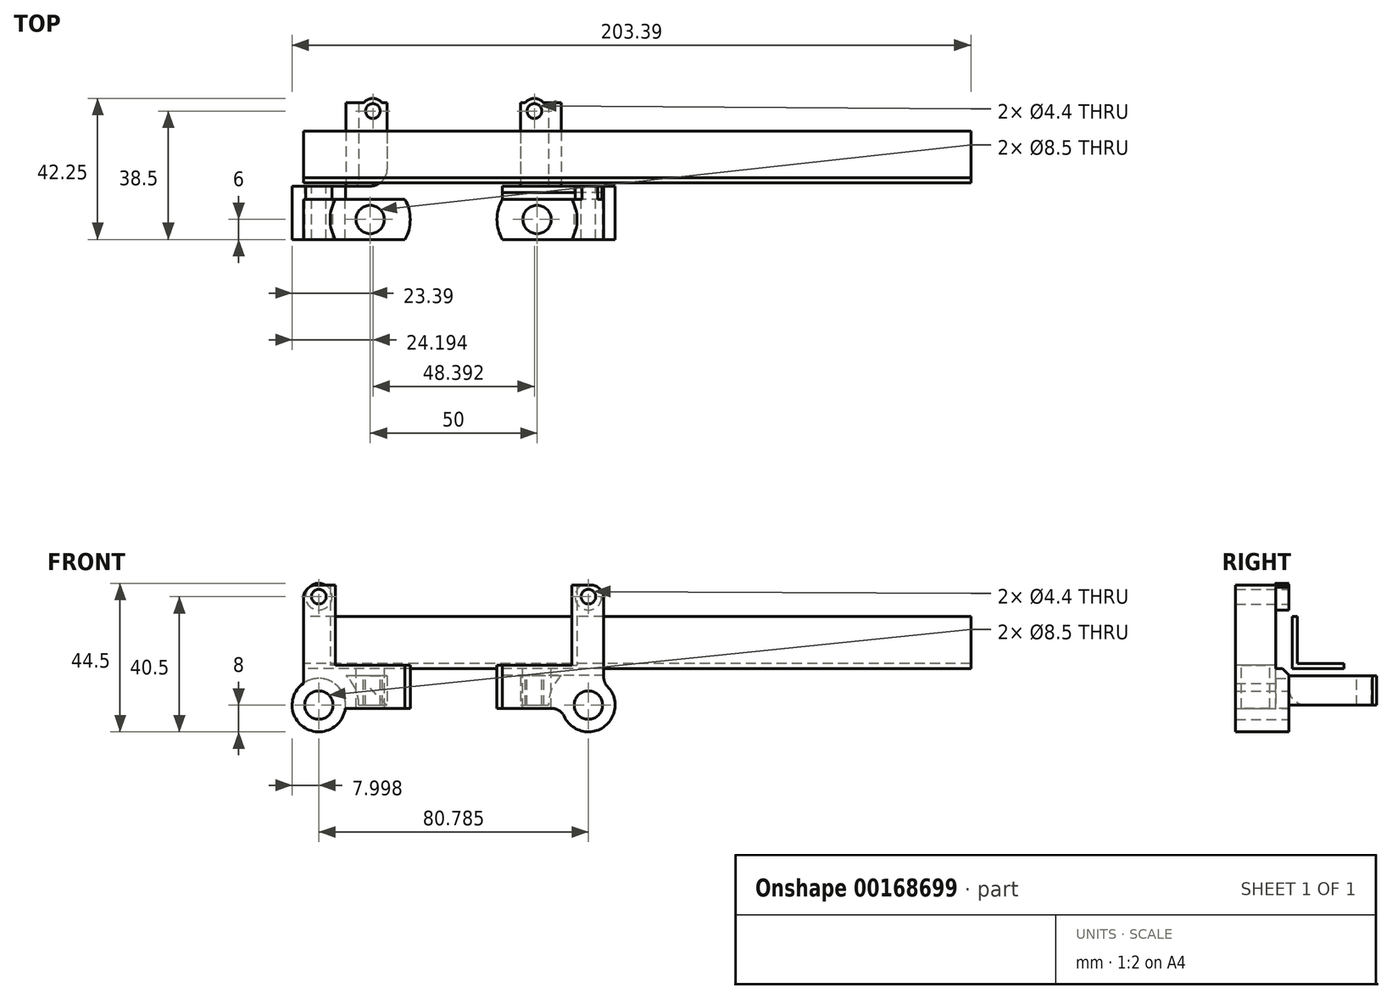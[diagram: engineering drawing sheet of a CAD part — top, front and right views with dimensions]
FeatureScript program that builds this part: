
annotation { "Feature Type Name" : "Feature", "Feature Type Description" : "" }
export const myFeature = defineFeature(function(context is Context, id is Id, definition is map)
    precondition{}
    {
        {
            var Q0;
            Q0=qCreatedBy(makeId("Right.planeOp"),FACE);
            var sketch = newSketch(context, id + "F0", { "sketchPlane" : qUnion([Q0])});
            skLineSegment(sketch, "E0", {"start": v(0, 0) * mm, "end": v(0, 15.5) * mm});
            skLineSegment(sketch, "E1", {"start": v(0, 15.5) * mm, "end": v(1.5, 15.5) * mm});
            skLineSegment(sketch, "E2", {"start": v(1.5, 15.5) * mm, "end": v(1.5, 1.5) * mm});
            skLineSegment(sketch, "E3", {"start": v(1.5, 1.5) * mm, "end": v(15.5, 1.5) * mm});
            skLineSegment(sketch, "E4", {"start": v(15.5, 1.5) * mm, "end": v(15.5, 0) * mm});
            skLineSegment(sketch, "E5", {"start": v(15.5, 0) * mm, "end": v(0, 0) * mm});
            skSolve(sketch);
        }
        {
            var Q0;
            Q0 = qSketchRegion(id + "F0", true);
            extrude(context, id + "F1", {"entities" : qUnion([Q0]), "depth" : 200 * mm, "offsetDistance" : 25 * mm});
        }
        {
            var Q0;
            Q0=qCreatedBy(makeId("Top.planeOp"),FACE);
            var sketch = newSketch(context, id + "F2", { "sketchPlane" : qUnion([Q0])});
            skCircle(sketch, "E6", {"center": v(20, -11) * mm, "radius": 11 * mm, "construction": true});
            skCircle(sketch, "E7", {"center": v(70, -11) * mm, "radius": 11 * mm, "construction": true});
            skCircle(sketch, "E8", {"center": v(20, -11) * mm, "radius": 4.25 * mm});
            skCircle(sketch, "E9", {"center": v(70, -11) * mm, "radius": 4.25 * mm});
            skLineSegment(sketch, "E10.bottom", {"start": v(0, -5) * mm, "end": v(90, -5) * mm});
            skLineSegment(sketch, "E10.top", {"start": v(0, -17) * mm, "end": v(90, -17) * mm});
            skLineSegment(sketch, "E10.left", {"start": v(0, -5) * mm, "end": v(0, -17) * mm});
            skLineSegment(sketch, "E10.right", {"start": v(90, -5) * mm, "end": v(90, -17) * mm});
            skPoint(sketch, "E10.middle", {"position": v(45, -11) * mm});
            skCircle(sketch, "E11", {"center": v(20, -11) * mm, "radius": 12 * mm});
            skCircle(sketch, "E12", {"center": v(70, -11) * mm, "radius": 12 * mm});
            skSolve(sketch);
        }
        {
            var Q0;
            {var subQ0=sQuery(id+"F2.wireOp",EDGE,"E10.left");Q0=makeQuery(id+"F2.imprint","IMPRINT",FACE,{"disambiguationData":[TD([[makeQuery(id+"F2.imprint","IMPRINT",EDGE,{"derivedFrom":subQ0}),1.0]])]});}
            var Q1;
            {var subQ0=sQuery(id+"F2.wireOp",EDGE,"E11");var subQ1=sQuery(id+"F2.wireOp",EDGE,"E10.bottom");var subQ2=makeQuery(id+"F2.imprint","INTERSECT",VERTEX,{"disambiguationData":[OD(1.0)],"derivedFrom":[subQ1,subQ0]});Q1=makeQuery(id+"F2.imprint","IMPRINT",FACE,{"disambiguationData":[TD([[makeQuery(id+"F2.imprint","IMPRINT",EDGE,{"disambiguationData":[TD([[subQ2,-1.0]])],"derivedFrom":subQ1}),-1.0]])]});}
            var Q2;
            {var subQ0=sQuery(id+"F2.wireOp",EDGE,"E10.right");Q2=makeQuery(id+"F2.imprint","IMPRINT",FACE,{"disambiguationData":[TD([[makeQuery(id+"F2.imprint","IMPRINT",EDGE,{"derivedFrom":subQ0}),-1.0]])]});}
            var Q3;
            Q3=makeQuery(id+"F2.imprint","IMPRINT",FACE,{"disambiguationData":[TD([[makeQuery(id+"F2.imprint","IMPRINT",EDGE,{"derivedFrom":sQuery(id+"F2.wireOp",EDGE,"E8")}),-1.0]])]});
            var Q4;
            Q4=makeQuery(id+"F2.imprint","IMPRINT",FACE,{"disambiguationData":[TD([[makeQuery(id+"F2.imprint","IMPRINT",EDGE,{"derivedFrom":sQuery(id+"F2.wireOp",EDGE,"E9")}),-1.0]])]});
            extrude(context, id + "F3", {"entities" : qUnion([Q0, Q1, Q2, Q3, Q4]), "oppositeDirection" : true, "depth" : 12 * mm, "offsetDistance" : 25 * mm, "hasSecondDirection" : true, "secondDirectionOppositeDirection" : false, "secondDirectionDepth" : 1 * mm});
        }
        {
            var Q0;
            {var subQ0=sQuery(id+"F2.wireOp",EDGE,"E10.left");Q0=makeQuery(id+"F2.imprint","IMPRINT",FACE,{"disambiguationData":[TD([[makeQuery(id+"F2.imprint","IMPRINT",EDGE,{"derivedFrom":subQ0}),1.0]])]});}
            var Q1;
            {var subQ0=sQuery(id+"F2.wireOp",EDGE,"E10.right");Q1=makeQuery(id+"F2.imprint","IMPRINT",FACE,{"disambiguationData":[TD([[makeQuery(id+"F2.imprint","IMPRINT",EDGE,{"derivedFrom":subQ0}),-1.0]])]});}
            extrude(context, id + "F4", {"entities" : qUnion([Q0, Q1]), "operationType" : NewBodyOperationType.ADD, "depth" : 25 * mm, "offsetDistance" : 25 * mm});
        }
        {
            var Q0;
            {var subQ0=sQuery(id+"F2.wireOp",EDGE,"E10.bottom");var subQ2=sQuery(id+"F2.wireOp",EDGE,"E11");Q0=makeQuery(id+"F4.boolean.opBoolean","MERGE",FACE,{"derivedFrom":[makeQuery(id+"F3.opExtrude","SWEPT_FACE",FACE,{"disambiguationData":[OSD([subQ0])]}),makeQuery(id+"F4.opExtrude","SWEPT_FACE",FACE,{"disambiguationData":[OSD([subQ0]),TDD([makeQuery(id+"F2.imprint","IMPRINT",EDGE,{"disambiguationData":[TD([[makeQuery(id+"F2.imprint","INTERSECT",VERTEX,{"derivedFrom":[subQ0,sQuery(id+"F2.wireOp",EDGE,"E10.left")]}),-1.0]])],"derivedFrom":subQ0})])]}),makeQuery(id+"F4.opExtrude","SWEPT_FACE",FACE,{"disambiguationData":[OSD([subQ0]),TDD([makeQuery(id+"F2.imprint","IMPRINT",EDGE,{"disambiguationData":[TD([[makeQuery(id+"F2.imprint","INTERSECT",VERTEX,{"disambiguationData":[OD(1.0)],"derivedFrom":[subQ0,subQ2]}),-1.0]])],"derivedFrom":subQ0})])]}),makeQuery(id+"F4.opExtrude","SWEPT_FACE",FACE,{"disambiguationData":[OSD([subQ0]),TDD([makeQuery(id+"F2.imprint","IMPRINT",EDGE,{"disambiguationData":[TD([[makeQuery(id+"F2.imprint","INTERSECT",VERTEX,{"derivedFrom":[subQ0,sQuery(id+"F2.wireOp",EDGE,"E10.right")]}),1.0]])],"derivedFrom":subQ0})])]})]});}
            var sketch = newSketch(context, id + "F5", { "sketchPlane" : qUnion([Q0])});
            skLineSegment(sketch, "E13.0.0", {"start": v(0, 1.5) * mm, "end": v(0, 15.5) * mm});
            skLineSegment(sketch, "E13.0.1", {"start": v(0, 15.5) * mm, "end": v(-200, 15.5) * mm});
            skLineSegment(sketch, "E13.0.2", {"start": v(-200, 15.5) * mm, "end": v(-200, 1.5) * mm});
            skLineSegment(sketch, "E13.0.3", {"start": v(-200, 1.5) * mm, "end": v(0, 1.5) * mm});
            skCircle(sketch, "E14", {"center": v(-4.6, 21.5) * mm, "radius": 6 * mm, "construction": true});
            skCircle(sketch, "E15", {"center": v(-4.6, 21.5) * mm, "radius": 2.2 * mm});
            skCircle(sketch, "E16", {"center": v(-85.4, 21.5) * mm, "radius": 6 * mm, "construction": true});
            skCircle(sketch, "E17", {"center": v(-85.4, 21.5) * mm, "radius": 2.2 * mm});
            skCircle(sketch, "E18", {"center": v(-4.6, 21.5) * mm, "radius": 4 * mm});
            skCircle(sketch, "E19", {"center": v(-85.4, 21.5) * mm, "radius": 4 * mm});
            skLineSegment(sketch, "E20.0", {"start": v(-200, 0) * mm, "end": v(0, 0) * mm});
            skCircle(sketch, "E21", {"center": v(-85.4, -11) * mm, "radius": 11 * mm, "construction": true});
            skCircle(sketch, "E22", {"center": v(-4.6, -11) * mm, "radius": 11 * mm, "construction": true});
            skCircle(sketch, "E23", {"center": v(-85.4, -11) * mm, "radius": 4.25 * mm});
            skCircle(sketch, "E24", {"center": v(-4.6, -11) * mm, "radius": 4.25 * mm});
            skCircle(sketch, "E25", {"center": v(-85.4, -11) * mm, "radius": 8 * mm});
            skCircle(sketch, "E26", {"center": v(-4.6, -11) * mm, "radius": 8 * mm});
            skSolve(sketch);
        }
        {
            var Q0;
            Q0=makeQuery(id+"F5.imprint","IMPRINT",FACE,{"disambiguationData":[TD([[makeQuery(id+"F5.imprint","IMPRINT",EDGE,{"derivedFrom":sQuery(id+"F5.wireOp",EDGE,"E15")}),1.0]])]});
            var Q1;
            Q1=makeQuery(id+"F5.imprint","IMPRINT",FACE,{"disambiguationData":[TD([[makeQuery(id+"F5.imprint","IMPRINT",EDGE,{"derivedFrom":sQuery(id+"F5.wireOp",EDGE,"E17")}),1.0]])]});
            extrude(context, id + "F6", {"entities" : qUnion([Q0, Q1]), "operationType" : NewBodyOperationType.REMOVE, "oppositeDirection" : true, "depth" : 25 * mm, "offsetDistance" : 25 * mm});
        }
        {
            var Q0;
            Q0=makeQuery(id+"F5.imprint","IMPRINT",FACE,{"disambiguationData":[TD([[makeQuery(id+"F5.imprint","IMPRINT",EDGE,{"derivedFrom":sQuery(id+"F5.wireOp",EDGE,"E15")}),-1.0]])]});
            var Q1;
            Q1=makeQuery(id+"F5.imprint","IMPRINT",FACE,{"disambiguationData":[TD([[makeQuery(id+"F5.imprint","IMPRINT",EDGE,{"derivedFrom":sQuery(id+"F5.wireOp",EDGE,"E17")}),-1.0]])]});
            extrude(context, id + "F7", {"entities" : qUnion([Q0, Q1]), "operationType" : NewBodyOperationType.ADD, "depth" : 4 * mm, "offsetDistance" : 25 * mm});
        }
        {
            var Q0;
            {var subQ1=sQuery(id+"F2.wireOp",EDGE,"E10.bottom");var subQ3=makeQuery(id+"F3.opExtrude","CAP_EDGE",EDGE,{"disambiguationData":[OSD([subQ1])],"isStart":false});var subQ8=sQuery(id+"F5.wireOp",EDGE,"E23");var subQ9=makeQuery(id+"F5.imprint","INTERSECT",VERTEX,{"disambiguationData":[OD(0.0)],"derivedFrom":[subQ3,subQ8]});Q0=makeQuery(id+"F5.imprint","IMPRINT",FACE,{"disambiguationData":[TD([[makeQuery(id+"F5.imprint","IMPRINT",EDGE,{"disambiguationData":[TD([[subQ9,-1.0]])],"derivedFrom":subQ8}),-1.0]])]});}
            var Q1;
            {var subQ1=sQuery(id+"F2.wireOp",EDGE,"E10.bottom");var subQ3=makeQuery(id+"F3.opExtrude","CAP_EDGE",EDGE,{"disambiguationData":[OSD([subQ1])],"isStart":false});var subQ7=sQuery(id+"F5.wireOp",EDGE,"E24");var subQ8=makeQuery(id+"F5.imprint","INTERSECT",VERTEX,{"disambiguationData":[OD(0.0)],"derivedFrom":[subQ3,subQ7]});Q1=makeQuery(id+"F5.imprint","IMPRINT",FACE,{"disambiguationData":[TD([[makeQuery(id+"F5.imprint","IMPRINT",EDGE,{"disambiguationData":[TD([[subQ8,1.0]])],"derivedFrom":subQ7}),-1.0]])]});}
            var Q2;
            {var subQ0=sQuery(id+"F2.wireOp",EDGE,"E10.top");Q2=makeQuery(id+"F4.boolean.opBoolean","MERGE",FACE,{"derivedFrom":[makeQuery(id+"F3.opExtrude","SWEPT_FACE",FACE,{"disambiguationData":[OSD([subQ0])]}),makeQuery(id+"F4.opExtrude","SWEPT_FACE",FACE,{"disambiguationData":[OSD([subQ0]),TDD([makeQuery(id+"F2.imprint","IMPRINT",EDGE,{"disambiguationData":[TD([[makeQuery(id+"F2.imprint","INTERSECT",VERTEX,{"derivedFrom":[subQ0,sQuery(id+"F2.wireOp",EDGE,"E10.left")]}),-1.0]])],"derivedFrom":subQ0})])]}),makeQuery(id+"F4.opExtrude","SWEPT_FACE",FACE,{"disambiguationData":[OSD([subQ0]),TDD([makeQuery(id+"F2.imprint","IMPRINT",EDGE,{"disambiguationData":[TD([[makeQuery(id+"F2.imprint","INTERSECT",VERTEX,{"derivedFrom":[subQ0,sQuery(id+"F2.wireOp",EDGE,"E10.right")]}),1.0]])],"derivedFrom":subQ0})])]})]});}
            extrude(context, id + "F8", {"entities" : qUnion([Q0, Q1]), "operationType" : NewBodyOperationType.ADD, "endBound" : BoundingType.UP_TO_SURFACE, "oppositeDirection" : true, "depth" : 25 * mm, "endBoundEntityFace" : qUnion([Q2]), "offsetDistance" : 25 * mm});
        }
        {
            var Q0;
            {var subQ0=sQuery(id+"F5.wireOp",EDGE,"E23");var subQ1=makeQuery(id+"F3.opExtrude","CAP_EDGE",EDGE,{"disambiguationData":[OSD([sQuery(id+"F2.wireOp",EDGE,"E10.bottom")])],"isStart":false});var subQ2=makeQuery(id+"F5.imprint","INTERSECT",VERTEX,{"disambiguationData":[OD(0.0)],"derivedFrom":[subQ1,subQ0]});Q0=makeQuery(id+"F5.imprint","IMPRINT",FACE,{"disambiguationData":[TD([[makeQuery(id+"F5.imprint","IMPRINT",EDGE,{"disambiguationData":[TD([[subQ2,1.0]])],"derivedFrom":subQ0}),1.0]])]});}
            var Q1;
            {var subQ0=sQuery(id+"F5.wireOp",EDGE,"E24");var subQ1=makeQuery(id+"F3.opExtrude","CAP_EDGE",EDGE,{"disambiguationData":[OSD([sQuery(id+"F2.wireOp",EDGE,"E10.bottom")])],"isStart":false});var subQ2=makeQuery(id+"F5.imprint","INTERSECT",VERTEX,{"disambiguationData":[OD(0.0)],"derivedFrom":[subQ1,subQ0]});Q1=makeQuery(id+"F5.imprint","IMPRINT",FACE,{"disambiguationData":[TD([[makeQuery(id+"F5.imprint","IMPRINT",EDGE,{"disambiguationData":[TD([[subQ2,-1.0]])],"derivedFrom":subQ0}),1.0]])]});}
            extrude(context, id + "F9", {"entities" : qUnion([Q0, Q1]), "operationType" : NewBodyOperationType.REMOVE, "oppositeDirection" : true, "depth" : 25 * mm, "offsetDistance" : 25 * mm});
        }
        {
            var Q0;
            {var subQ0=sQuery(id+"F5.wireOp",EDGE,"E25");var subQ1=sQuery(id+"F2.wireOp",EDGE,"E10.bottom");var subQ2=makeQuery(id+"F3.opExtrude","CAP_EDGE",EDGE,{"disambiguationData":[OSD([subQ1])],"isStart":false});var subQ3=makeQuery(id+"F5.imprint","INTERSECT",VERTEX,{"derivedFrom":[subQ2,subQ0]});Q0=makeQuery(id+"F5.imprint","IMPRINT",FACE,{"disambiguationData":[TD([[makeQuery(id+"F5.imprint","IMPRINT",EDGE,{"disambiguationData":[TD([[subQ3,1.0]])],"derivedFrom":subQ2}),-1.0]])]});}
            var Q1;
            {var subQ1=sQuery(id+"F2.wireOp",EDGE,"E10.bottom");var subQ3=makeQuery(id+"F3.opExtrude","CAP_EDGE",EDGE,{"disambiguationData":[OSD([subQ1])],"isStart":false});var subQ7=sQuery(id+"F5.wireOp",EDGE,"E23");var subQ8=makeQuery(id+"F5.imprint","INTERSECT",VERTEX,{"disambiguationData":[OD(0.0)],"derivedFrom":[subQ3,subQ7]});Q1=makeQuery(id+"F5.imprint","IMPRINT",FACE,{"disambiguationData":[TD([[makeQuery(id+"F5.imprint","IMPRINT",EDGE,{"disambiguationData":[TD([[subQ8,1.0]])],"derivedFrom":subQ7}),-1.0]])]});}
            var Q2;
            {var subQ1=sQuery(id+"F2.wireOp",EDGE,"E10.bottom");var subQ3=makeQuery(id+"F3.opExtrude","CAP_EDGE",EDGE,{"disambiguationData":[OSD([subQ1])],"isStart":false});var subQ8=sQuery(id+"F5.wireOp",EDGE,"E23");var subQ9=makeQuery(id+"F5.imprint","INTERSECT",VERTEX,{"disambiguationData":[OD(0.0)],"derivedFrom":[subQ3,subQ8]});Q2=makeQuery(id+"F5.imprint","IMPRINT",FACE,{"disambiguationData":[TD([[makeQuery(id+"F5.imprint","IMPRINT",EDGE,{"disambiguationData":[TD([[subQ9,-1.0]])],"derivedFrom":subQ8}),-1.0]])]});}
            var Q3;
            {var subQ1=sQuery(id+"F2.wireOp",EDGE,"E10.bottom");var subQ3=makeQuery(id+"F3.opExtrude","CAP_EDGE",EDGE,{"disambiguationData":[OSD([subQ1])],"isStart":false});var subQ5=sQuery(id+"F5.wireOp",EDGE,"E24");var subQ6=makeQuery(id+"F5.imprint","INTERSECT",VERTEX,{"disambiguationData":[OD(0.0)],"derivedFrom":[subQ3,subQ5]});Q3=makeQuery(id+"F5.imprint","IMPRINT",FACE,{"disambiguationData":[TD([[makeQuery(id+"F5.imprint","IMPRINT",EDGE,{"disambiguationData":[TD([[subQ6,-1.0]])],"derivedFrom":subQ5}),-1.0]])]});}
            var Q4;
            {var subQ1=sQuery(id+"F2.wireOp",EDGE,"E10.bottom");var subQ3=makeQuery(id+"F3.opExtrude","CAP_EDGE",EDGE,{"disambiguationData":[OSD([subQ1])],"isStart":false});var subQ7=sQuery(id+"F5.wireOp",EDGE,"E24");var subQ8=makeQuery(id+"F5.imprint","INTERSECT",VERTEX,{"disambiguationData":[OD(0.0)],"derivedFrom":[subQ3,subQ7]});Q4=makeQuery(id+"F5.imprint","IMPRINT",FACE,{"disambiguationData":[TD([[makeQuery(id+"F5.imprint","IMPRINT",EDGE,{"disambiguationData":[TD([[subQ8,1.0]])],"derivedFrom":subQ7}),-1.0]])]});}
            extrude(context, id + "F10", {"entities" : qUnion([Q0, Q1, Q2, Q3, Q4]), "operationType" : NewBodyOperationType.ADD, "depth" : 4 * mm, "offsetDistance" : 25 * mm});
        }
        {
            var Q0;
            Q0=makeQuery(id+"F10.opExtrude","CAP_FACE",FACE,{"disambiguationData":[OSD([sQuery(id+"F2.wireOp",EDGE,"E10.bottom"),sQuery(id+"F2.wireOp",EDGE,"E10.left"),sQuery(id+"F2.wireOp",EDGE,"E10.right"),sQuery(id+"F5.wireOp",EDGE,"E20.0"),sQuery(id+"F5.wireOp",EDGE,"E23"),sQuery(id+"F5.wireOp",EDGE,"E24"),sQuery(id+"F5.wireOp",EDGE,"E25"),sQuery(id+"F5.wireOp",EDGE,"E26")])],"isStart":false});
            var sketch = newSketch(context, id + "F11", { "sketchPlane" : qUnion([Q0])});
            skCircle(sketch, "E27", {"center": v(-85.4, -11) * mm, "radius": 12 * mm});
            skCircle(sketch, "E28", {"center": v(-4.6, -11) * mm, "radius": 12 * mm});
            skLineSegment(sketch, "E29.top", {"start": v(-85.4, -2.23) * mm, "end": v(0, -2.23) * mm});
            skLineSegment(sketch, "E29.left", {"start": v(-85.4, -11) * mm, "end": v(-85.4, -2.23) * mm});
            skLineSegment(sketch, "E29.right", {"start": v(0, -11) * mm, "end": v(0, -2.23) * mm});
            skLineSegment(sketch, "E30", {"start": v(-4.6, -11) * mm, "end": v(-4.6, -2.23) * mm});
            skLineSegment(sketch, "E31", {"start": v(-4.6, -11) * mm, "end": v(-85.4, -11) * mm});
            skLineSegment(sketch, "E32.bottom", {"start": v(-65, -2.23) * mm, "end": v(-25, -2.23) * mm});
            skLineSegment(sketch, "E32.top", {"start": v(-65, -11) * mm, "end": v(-25, -11) * mm});
            skLineSegment(sketch, "E32.left", {"start": v(-65, -2.23) * mm, "end": v(-65, -11) * mm});
            skLineSegment(sketch, "E32.right", {"start": v(-25, -2.23) * mm, "end": v(-25, -11) * mm});
            skPoint(sketch, "E32.middle", {"position": v(-45, -6.62) * mm});
            skPoint(sketch, "E32.middle.positionSnap0", {"position": v(-85.4, -6.62) * mm});
            skPoint(sketch, "E32.middle.positionSnap1", {"position": v(-45, -11) * mm});
            skPoint(sketch, "E32.centerSnap0", {"position": v(-85.4, -6.62) * mm});
            skPoint(sketch, "E32.centerSnap1", {"position": v(-45, -11) * mm});
            skSolve(sketch);
        }
        {
            var Q0;
            {var subQ5=sQuery(id+"F11.wireOp",EDGE,"E32.left");Q0=makeQuery(id+"F11.imprint","IMPRINT",FACE,{"disambiguationData":[TD([[makeQuery(id+"F11.imprint","IMPRINT",EDGE,{"derivedFrom":subQ5}),-1.0]])]});}
            var Q1;
            {var subQ5=sQuery(id+"F11.wireOp",EDGE,"E32.right");Q1=makeQuery(id+"F11.imprint","IMPRINT",FACE,{"disambiguationData":[TD([[makeQuery(id+"F11.imprint","IMPRINT",EDGE,{"derivedFrom":subQ5}),1.0]])]});}
            extrude(context, id + "F12", {"entities" : qUnion([Q0, Q1]), "operationType" : NewBodyOperationType.ADD, "depth" : 25 * mm, "offsetDistance" : 25 * mm});
        }
        {
            var Q0;
            {var subQ0=sQuery(id+"F11.wireOp",EDGE,"E29.top");Q0=makeQuery(id+"F12.opExtrude","SWEPT_FACE",FACE,{"disambiguationData":[OSD([subQ0]),TDD([makeQuery(id+"F11.imprint","IMPRINT",EDGE,{"disambiguationData":[TD([[makeQuery(id+"F11.imprint","INTERSECT",VERTEX,{"derivedFrom":[subQ0,sQuery(id+"F11.wireOp",EDGE,"E32.left")]}),1.0]])],"derivedFrom":subQ0})])]});}
            var sketch = newSketch(context, id + "F13", { "sketchPlane" : qUnion([Q0])});
            skLineSegment(sketch, "E33.0.0", {"start": v(73.4, -1) * mm, "end": v(65, -1) * mm});
            skLineSegment(sketch, "E33.0.1", {"start": v(65, -1) * mm, "end": v(65, 24) * mm});
            skLineSegment(sketch, "E33.0.2", {"start": v(65, 24) * mm, "end": v(73.4, 24) * mm});
            skLineSegment(sketch, "E33.0.3", {"start": v(73.4, 24) * mm, "end": v(73.4, -1) * mm});
            skLineSegment(sketch, "E34.0.0", {"start": v(25, -1) * mm, "end": v(16.6, -1) * mm});
            skLineSegment(sketch, "E34.0.1", {"start": v(16.6, -1) * mm, "end": v(16.6, 24) * mm});
            skLineSegment(sketch, "E34.0.2", {"start": v(16.6, 24) * mm, "end": v(25, 24) * mm});
            skLineSegment(sketch, "E34.0.3", {"start": v(25, 24) * mm, "end": v(25, -1) * mm});
            skLineSegment(sketch, "E35.0", {"start": v(200, 15.5) * mm, "end": v(0, 15.5) * mm});
            skCircle(sketch, "E36", {"center": v(20.8, 21.5) * mm, "radius": 6 * mm, "construction": true});
            skPoint(sketch, "E36.centerSnap0", {"position": v(20.8, 24) * mm});
            skCircle(sketch, "E37", {"center": v(69.2, 21.5) * mm, "radius": 6 * mm, "construction": true});
            skPoint(sketch, "E37.centerSnap0", {"position": v(69.2, 24) * mm});
            skCircle(sketch, "E38", {"center": v(20.8, 21.5) * mm, "radius": 3.75 * mm});
            skCircle(sketch, "E39", {"center": v(69.2, 21.5) * mm, "radius": 3.75 * mm});
            skCircle(sketch, "E40", {"center": v(20.8, 21.5) * mm, "radius": 2.2 * mm});
            skCircle(sketch, "E41", {"center": v(69.2, 21.5) * mm, "radius": 2.2 * mm});
            skSolve(sketch);
        }
        {
            var Q0;
            {var subQ0=sQuery(id+"F13.wireOp",EDGE,"E38");var subQ1=sQuery(id+"F13.wireOp",EDGE,"E34.0.2");var subQ2=makeQuery(id+"F13.imprint","INTERSECT",VERTEX,{"disambiguationData":[OD(0.0)],"derivedFrom":[subQ1,subQ0]});Q0=makeQuery(id+"F13.imprint","IMPRINT",FACE,{"disambiguationData":[TD([[makeQuery(id+"F13.imprint","IMPRINT",EDGE,{"disambiguationData":[TD([[subQ2,-1.0]])],"derivedFrom":subQ1}),1.0]])]});}
            var Q1;
            {var subQ0=sQuery(id+"F13.wireOp",EDGE,"E39");var subQ1=sQuery(id+"F13.wireOp",EDGE,"E33.0.2");var subQ2=makeQuery(id+"F13.imprint","INTERSECT",VERTEX,{"disambiguationData":[OD(0.0)],"derivedFrom":[subQ1,subQ0]});Q1=makeQuery(id+"F13.imprint","IMPRINT",FACE,{"disambiguationData":[TD([[makeQuery(id+"F13.imprint","IMPRINT",EDGE,{"disambiguationData":[TD([[subQ2,-1.0]])],"derivedFrom":subQ1}),-1.0]])]});}
            var Q2;
            {var subQ0=sQuery(id+"F11.wireOp",EDGE,"E31");Q2=makeQuery(id+"F12.opExtrude","SWEPT_FACE",FACE,{"disambiguationData":[OSD([subQ0]),TDD([makeQuery(id+"F11.imprint","IMPRINT",EDGE,{"disambiguationData":[TD([[makeQuery(id+"F11.imprint","INTERSECT",VERTEX,{"derivedFrom":[subQ0,sQuery(id+"F11.wireOp",EDGE,"E32.right")]}),1.0]])],"derivedFrom":subQ0})])]});}
            extrude(context, id + "F14", {"entities" : qUnion([Q0, Q1]), "operationType" : NewBodyOperationType.ADD, "endBound" : BoundingType.UP_TO_SURFACE, "oppositeDirection" : true, "depth" : 25 * mm, "endBoundEntityFace" : qUnion([Q2]), "offsetDistance" : 25 * mm});
        }
        {
            var Q0;
            Q0=makeQuery(id+"F13.imprint","IMPRINT",FACE,{"disambiguationData":[TD([[makeQuery(id+"F13.imprint","IMPRINT",EDGE,{"derivedFrom":sQuery(id+"F13.wireOp",EDGE,"E40")}),1.0]])]});
            var Q1;
            Q1=makeQuery(id+"F13.imprint","IMPRINT",FACE,{"disambiguationData":[TD([[makeQuery(id+"F13.imprint","IMPRINT",EDGE,{"derivedFrom":sQuery(id+"F13.wireOp",EDGE,"E41")}),1.0]])]});
            extrude(context, id + "F15", {"entities" : qUnion([Q0, Q1]), "operationType" : NewBodyOperationType.REMOVE, "oppositeDirection" : true, "depth" : 25 * mm, "offsetDistance" : 25 * mm});
        }
        {
            var Q0;
            Q0=makeQuery(id+"F12.opExtrude","CAP_EDGE",EDGE,{"disambiguationData":[OSD([sQuery(id+"F11.wireOp",EDGE,"E32.left")])],"isStart":true});
            var Q1;
            Q1=makeQuery(id+"F12.opExtrude","CAP_EDGE",EDGE,{"disambiguationData":[OSD([sQuery(id+"F11.wireOp",EDGE,"E32.right")])],"isStart":true});
            var Q2;
            {var subQ0=sQuery(id+"F11.wireOp",EDGE,"E31");Q2=makeQuery(id+"F12.opExtrude","CAP_EDGE",EDGE,{"disambiguationData":[OSD([subQ0]),TDD([makeQuery(id+"F11.imprint","IMPRINT",EDGE,{"disambiguationData":[TD([[makeQuery(id+"F11.imprint","INTERSECT",VERTEX,{"derivedFrom":[subQ0,sQuery(id+"F11.wireOp",EDGE,"E32.left")]}),-1.0]])],"derivedFrom":subQ0})])],"isStart":true});}
            var Q3;
            {var subQ0=sQuery(id+"F11.wireOp",EDGE,"E31");Q3=makeQuery(id+"F12.opExtrude","CAP_EDGE",EDGE,{"disambiguationData":[OSD([subQ0]),TDD([makeQuery(id+"F11.imprint","IMPRINT",EDGE,{"disambiguationData":[TD([[makeQuery(id+"F11.imprint","INTERSECT",VERTEX,{"derivedFrom":[subQ0,sQuery(id+"F11.wireOp",EDGE,"E32.right")]}),1.0]])],"derivedFrom":subQ0})])],"isStart":true});}
            fillet(context, id + "F16", {"entities" : qUnion([Q0, Q1, Q2, Q3]), "radius" : 5 * mm, "tangentPropagation" : true, "allowEdgeOverflow" : false});
        }
        {
            var Q0;
            Q0=makeQuery(id+"F10.opExtrude","CAP_EDGE",EDGE,{"disambiguationData":[OSD([sQuery(id+"F5.wireOp",EDGE,"E20.0")])],"isStart":false});
            chamfer(context, id + "F17", {"entities" : qUnion([Q0]), "width" : 2 * mm, "tangentPropagation" : true});
        }
        {
            var Q0;
            {var subQ0=sQuery(id+"F5.wireOp",EDGE,"E26");var subQ1=sQuery(id+"F2.wireOp",EDGE,"E10.left");var subQ2=sQuery(id+"F2.wireOp",EDGE,"E10.bottom");Q0=makeQuery(id+"F10.boolean.opBoolean","MERGE",EDGE,{"derivedFrom":[makeQuery(id+"F8.opExtrude","SWEPT_EDGE",EDGE,{"disambiguationData":[OSD([subQ2,subQ1,subQ0])]}),makeQuery(id+"F10.opExtrude","SWEPT_EDGE",EDGE,{"disambiguationData":[OSD([subQ2,subQ1,subQ0])]})]});}
            var Q1;
            {var subQ0=sQuery(id+"F5.wireOp",EDGE,"E25");var subQ1=sQuery(id+"F2.wireOp",EDGE,"E10.right");var subQ2=sQuery(id+"F2.wireOp",EDGE,"E10.bottom");Q1=makeQuery(id+"F10.boolean.opBoolean","MERGE",EDGE,{"derivedFrom":[makeQuery(id+"F8.opExtrude","SWEPT_EDGE",EDGE,{"disambiguationData":[OSD([subQ2,subQ1,subQ0])]}),makeQuery(id+"F10.opExtrude","SWEPT_EDGE",EDGE,{"disambiguationData":[OSD([subQ2,subQ1,subQ0])]})]});}
            var Q2;
            Q2=makeQuery(id+"F4.opExtrude","CAP_EDGE",EDGE,{"disambiguationData":[OSD([sQuery(id+"F2.wireOp",EDGE,"E10.right")])],"isStart":false});
            var Q3;
            Q3=makeQuery(id+"F4.opExtrude","CAP_EDGE",EDGE,{"disambiguationData":[OSD([sQuery(id+"F2.wireOp",EDGE,"E10.left")])],"isStart":false});
            fillet(context, id + "F18", {"entities" : qUnion([Q0, Q1, Q2, Q3]), "radius" : 4 * mm, "tangentPropagation" : true, "allowEdgeOverflow" : false});
        }
    });
